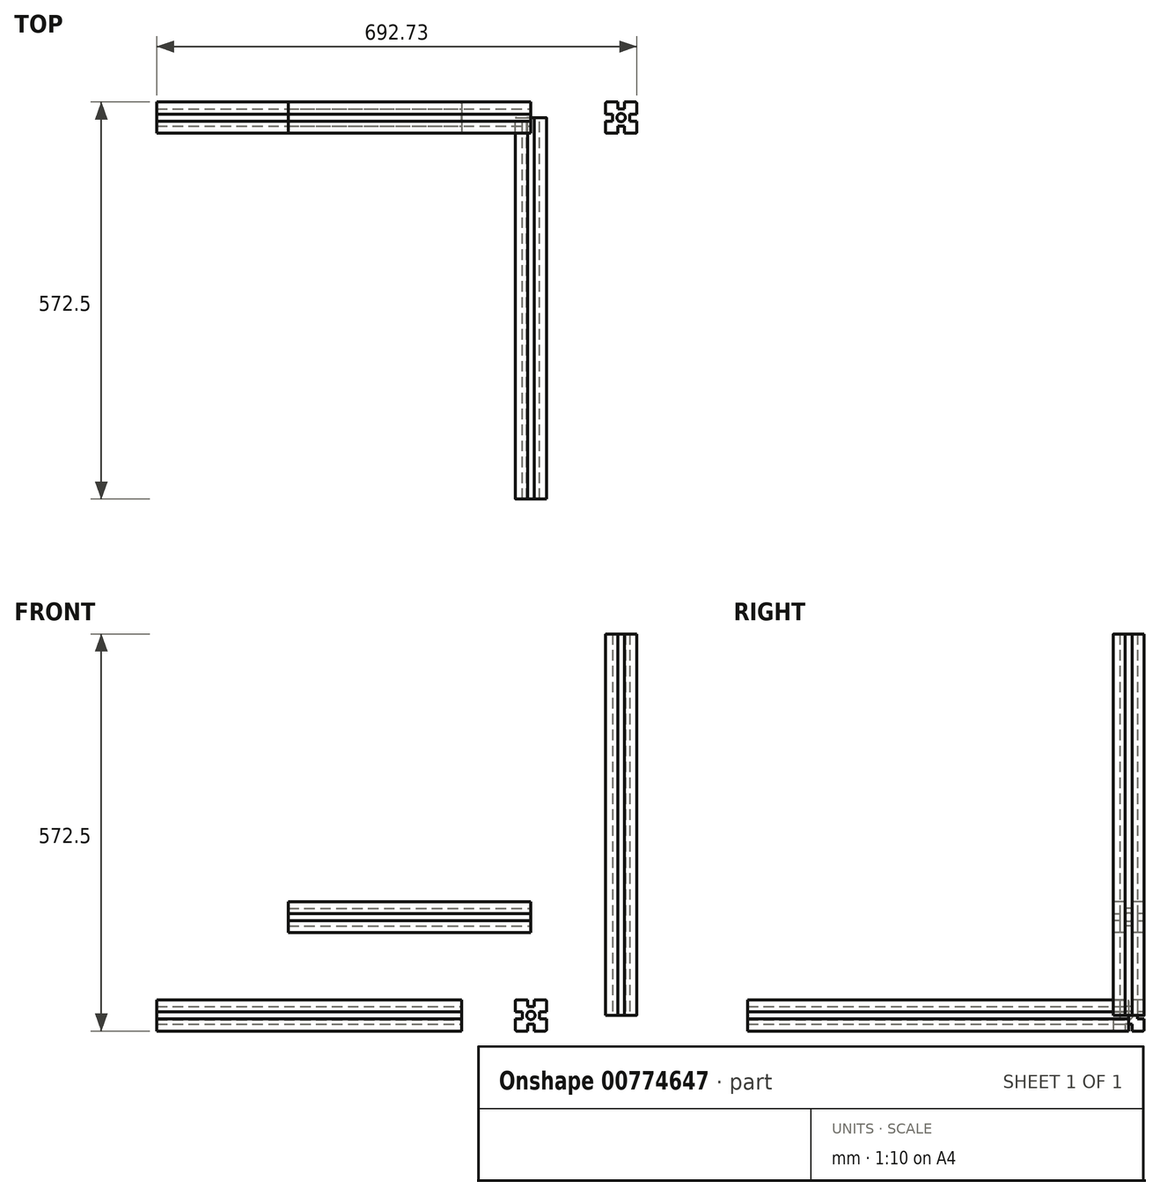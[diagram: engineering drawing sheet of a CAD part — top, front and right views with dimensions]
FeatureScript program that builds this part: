
annotation { "Feature Type Name" : "Feature", "Feature Type Description" : "" }
export const myFeature = defineFeature(function(context is Context, id is Id, definition is map)
    precondition{}
    {
        {
            var Q0;
            Q0=qCreatedBy(makeId("Front.planeOp"),FACE);
            var sketch = newSketch(context, id + "F0", { "sketchPlane" : qUnion([Q0])});
            skLineSegment(sketch, "E0.bottom", {"start": v(-20.5, 22.5) * mm, "end": v(-5, 22.5) * mm});
            skLineSegment(sketch, "E0.top", {"start": v(-20.5, -22.5) * mm, "end": v(-5, -22.5) * mm});
            skLineSegment(sketch, "E0.left", {"start": v(-22.5, 20.5) * mm, "end": v(-22.5, 5) * mm});
            skLineSegment(sketch, "E0.right", {"start": v(22.5, 20.5) * mm, "end": v(22.5, 5) * mm});
            skPoint(sketch, "E1.visualSharp", {"position": v(-22.5, 22.5) * mm});
            skArc(sketch, "E1.filletArc", {"start": v(-20.5, 22.5) * mm, "mid": v(-21.91, 21.91) * mm, "end": v(-22.5, 20.5) * mm});
            skPoint(sketch, "E2.visualSharp", {"position": v(22.5, 22.5) * mm});
            skArc(sketch, "E2.filletArc", {"start": v(22.5, 20.5) * mm, "mid": v(21.91, 21.91) * mm, "end": v(20.5, 22.5) * mm});
            skPoint(sketch, "E3.visualSharp", {"position": v(22.5, -22.5) * mm});
            skArc(sketch, "E3.filletArc", {"start": v(20.5, -22.5) * mm, "mid": v(21.91, -21.91) * mm, "end": v(22.5, -20.5) * mm});
            skPoint(sketch, "E4.visualSharp", {"position": v(-22.5, -22.5) * mm});
            skArc(sketch, "E4.filletArc", {"start": v(-22.5, -20.5) * mm, "mid": v(-21.91, -21.91) * mm, "end": v(-20.5, -22.5) * mm});
            skLineSegment(sketch, "E5", {"start": v(-5, 22.5) * mm, "end": v(-5, 12.5) * mm});
            skLineSegment(sketch, "E6", {"start": v(-5, 12.5) * mm, "end": v(5, 12.5) * mm});
            skLineSegment(sketch, "E7", {"start": v(5, 12.5) * mm, "end": v(5, 22.5) * mm});
            skLineSegment(sketch, "E8", {"start": v(-22.5, 5) * mm, "end": v(-12.5, 5) * mm});
            skLineSegment(sketch, "E9", {"start": v(-12.5, 5) * mm, "end": v(-12.5, -5) * mm});
            skLineSegment(sketch, "E10", {"start": v(-12.5, -5) * mm, "end": v(-22.5, -5) * mm});
            skLineSegment(sketch, "E11", {"start": v(-5, -22.5) * mm, "end": v(-5, -12.5) * mm});
            skLineSegment(sketch, "E12", {"start": v(-5, -12.5) * mm, "end": v(5, -12.5) * mm});
            skLineSegment(sketch, "E13", {"start": v(5, -12.5) * mm, "end": v(5, -22.5) * mm});
            skLineSegment(sketch, "E14", {"start": v(22.5, 5) * mm, "end": v(12.5, 5) * mm});
            skLineSegment(sketch, "E15", {"start": v(12.5, 5) * mm, "end": v(12.5, -5) * mm});
            skLineSegment(sketch, "E16", {"start": v(12.5, -5) * mm, "end": v(22.5, -5) * mm});
            skCircle(sketch, "E17", {"center": v(0, 0) * mm, "radius": 6 * mm});
            skLineSegment(sketch, "E18.trimOffspring", {"start": v(5, 22.5) * mm, "end": v(20.5, 22.5) * mm});
            skLineSegment(sketch, "E19.trimOffspring", {"start": v(22.5, -5) * mm, "end": v(22.5, -20.5) * mm});
            skLineSegment(sketch, "E20.trimOffspring", {"start": v(5, -22.5) * mm, "end": v(20.5, -22.5) * mm});
            skLineSegment(sketch, "E21.trimOffspring", {"start": v(-22.5, -5) * mm, "end": v(-22.5, -20.5) * mm});
            skSolve(sketch);
        }
        {
            var Q0;
            Q0 = qSketchRegion(id + "F0", true);
            extrude(context, id + "F1", {"entities" : qUnion([Q0]), "depth" : 350 * mm, "offsetDistance" : 25 * mm});
        }
        {
            var Q0;
            Q0 = qSketchRegion(id + "F0", true);
            extrude(context, id + "F2", {"entities" : qUnion([Q0]), "depth" : 550 * mm, "offsetDistance" : 25 * mm});
        }
        {
            var Q0;
            Q0=qCreatedBy(makeId("Front.planeOp"),FACE);
            var sketch = newSketch(context, id + "F3", { "sketchPlane" : qUnion([Q0])});
            skLineSegment(sketch, "E22", {"start": v(0, 71.55) * mm, "end": v(0, -70.15) * mm, "construction": true});
            skLineSegment(sketch, "E23", {"start": v(-68.62, 0) * mm, "end": v(61.61, 0) * mm, "construction": true});
            skSolve(sketch);
        }
        {
            var Q0;
            Q0=makeQuery(id+"F1.opExtrude","SWEPT_BODY",BODY,{"disambiguationData":[OSD([sQuery(id+"F0.wireOp",EDGE,"E0.bottom"),sQuery(id+"F0.wireOp",EDGE,"E0.top"),sQuery(id+"F0.wireOp",EDGE,"E0.left"),sQuery(id+"F0.wireOp",EDGE,"E0.right"),sQuery(id+"F0.wireOp",EDGE,"E1.filletArc"),sQuery(id+"F0.wireOp",EDGE,"E2.filletArc"),sQuery(id+"F0.wireOp",EDGE,"E3.filletArc"),sQuery(id+"F0.wireOp",EDGE,"E4.filletArc"),sQuery(id+"F0.wireOp",EDGE,"E5"),sQuery(id+"F0.wireOp",EDGE,"E6"),sQuery(id+"F0.wireOp",EDGE,"E7"),sQuery(id+"F0.wireOp",EDGE,"E8"),sQuery(id+"F0.wireOp",EDGE,"E9"),sQuery(id+"F0.wireOp",EDGE,"E10"),sQuery(id+"F0.wireOp",EDGE,"E11"),sQuery(id+"F0.wireOp",EDGE,"E12"),sQuery(id+"F0.wireOp",EDGE,"E13"),sQuery(id+"F0.wireOp",EDGE,"E14"),sQuery(id+"F0.wireOp",EDGE,"E15"),sQuery(id+"F0.wireOp",EDGE,"E16"),sQuery(id+"F0.wireOp",EDGE,"E17"),sQuery(id+"F0.wireOp",EDGE,"E18.trimOffspring"),sQuery(id+"F0.wireOp",EDGE,"E19.trimOffspring"),sQuery(id+"F0.wireOp",EDGE,"E20.trimOffspring"),sQuery(id+"F0.wireOp",EDGE,"E21.trimOffspring")])]});
            var Q1;
            Q1=sQuery(id+"F3.wireOp",EDGE,"E22");
            transform(context, id + "F4", {"entities" : qUnion([Q0]), "transformType" : TransformType.ROTATION, "transformAxis" : qUnion([Q1]), "angle" : 90 * degree, "makeCopy" : false});
        }
        {
            var Q0;
            Q0=makeQuery(id+"F1.opExtrude","SWEPT_BODY",BODY,{"disambiguationData":[OSD([sQuery(id+"F0.wireOp",EDGE,"E0.bottom"),sQuery(id+"F0.wireOp",EDGE,"E0.top"),sQuery(id+"F0.wireOp",EDGE,"E0.left"),sQuery(id+"F0.wireOp",EDGE,"E0.right"),sQuery(id+"F0.wireOp",EDGE,"E1.filletArc"),sQuery(id+"F0.wireOp",EDGE,"E2.filletArc"),sQuery(id+"F0.wireOp",EDGE,"E3.filletArc"),sQuery(id+"F0.wireOp",EDGE,"E4.filletArc"),sQuery(id+"F0.wireOp",EDGE,"E5"),sQuery(id+"F0.wireOp",EDGE,"E6"),sQuery(id+"F0.wireOp",EDGE,"E7"),sQuery(id+"F0.wireOp",EDGE,"E8"),sQuery(id+"F0.wireOp",EDGE,"E9"),sQuery(id+"F0.wireOp",EDGE,"E10"),sQuery(id+"F0.wireOp",EDGE,"E11"),sQuery(id+"F0.wireOp",EDGE,"E12"),sQuery(id+"F0.wireOp",EDGE,"E13"),sQuery(id+"F0.wireOp",EDGE,"E14"),sQuery(id+"F0.wireOp",EDGE,"E15"),sQuery(id+"F0.wireOp",EDGE,"E16"),sQuery(id+"F0.wireOp",EDGE,"E17"),sQuery(id+"F0.wireOp",EDGE,"E18.trimOffspring"),sQuery(id+"F0.wireOp",EDGE,"E19.trimOffspring"),sQuery(id+"F0.wireOp",EDGE,"E20.trimOffspring"),sQuery(id+"F0.wireOp",EDGE,"E21.trimOffspring")])]});
            var Q1;
            Q1=sQuery(id+"F3.wireOp",EDGE,"E22");
            transform(context, id + "F5", {"entities" : qUnion([Q0]), "transformType" : TransformType.TRANSLATION_ENTITY, "oppositeDirectionEntity" : true, "transformLine" : qUnion([Q1]), "makeCopy" : false});
        }
        {
            var Q0;
            Q0 = qSketchRegion(id + "F0", true);
            extrude(context, id + "F6", {"entities" : qUnion([Q0]), "depth" : 550 * mm, "offsetDistance" : 25 * mm});
        }
        {
            var Q0;
            Q0=makeQuery(id+"F6.opExtrude","SWEPT_BODY",BODY,{"disambiguationData":[OSD([sQuery(id+"F0.wireOp",EDGE,"E0.bottom"),sQuery(id+"F0.wireOp",EDGE,"E0.top"),sQuery(id+"F0.wireOp",EDGE,"E0.left"),sQuery(id+"F0.wireOp",EDGE,"E0.right"),sQuery(id+"F0.wireOp",EDGE,"E1.filletArc"),sQuery(id+"F0.wireOp",EDGE,"E2.filletArc"),sQuery(id+"F0.wireOp",EDGE,"E3.filletArc"),sQuery(id+"F0.wireOp",EDGE,"E4.filletArc"),sQuery(id+"F0.wireOp",EDGE,"E5"),sQuery(id+"F0.wireOp",EDGE,"E6"),sQuery(id+"F0.wireOp",EDGE,"E7"),sQuery(id+"F0.wireOp",EDGE,"E8"),sQuery(id+"F0.wireOp",EDGE,"E9"),sQuery(id+"F0.wireOp",EDGE,"E10"),sQuery(id+"F0.wireOp",EDGE,"E11"),sQuery(id+"F0.wireOp",EDGE,"E12"),sQuery(id+"F0.wireOp",EDGE,"E13"),sQuery(id+"F0.wireOp",EDGE,"E14"),sQuery(id+"F0.wireOp",EDGE,"E15"),sQuery(id+"F0.wireOp",EDGE,"E16"),sQuery(id+"F0.wireOp",EDGE,"E17"),sQuery(id+"F0.wireOp",EDGE,"E18.trimOffspring"),sQuery(id+"F0.wireOp",EDGE,"E19.trimOffspring"),sQuery(id+"F0.wireOp",EDGE,"E20.trimOffspring"),sQuery(id+"F0.wireOp",EDGE,"E21.trimOffspring")])]});
            var Q1;
            Q1=sQuery(id+"F3.wireOp",EDGE,"E23");
            transform(context, id + "F7", {"entities" : qUnion([Q0]), "transformType" : TransformType.ROTATION, "transformAxis" : qUnion([Q1]), "angle" : 90 * degree, "oppositeDirection" : true, "makeCopy" : false});
        }
        {
            var Q0;
            Q0=makeQuery(id+"F6.opExtrude","SWEPT_BODY",BODY,{"disambiguationData":[OSD([sQuery(id+"F0.wireOp",EDGE,"E0.bottom"),sQuery(id+"F0.wireOp",EDGE,"E0.top"),sQuery(id+"F0.wireOp",EDGE,"E0.left"),sQuery(id+"F0.wireOp",EDGE,"E0.right"),sQuery(id+"F0.wireOp",EDGE,"E1.filletArc"),sQuery(id+"F0.wireOp",EDGE,"E2.filletArc"),sQuery(id+"F0.wireOp",EDGE,"E3.filletArc"),sQuery(id+"F0.wireOp",EDGE,"E4.filletArc"),sQuery(id+"F0.wireOp",EDGE,"E5"),sQuery(id+"F0.wireOp",EDGE,"E6"),sQuery(id+"F0.wireOp",EDGE,"E7"),sQuery(id+"F0.wireOp",EDGE,"E8"),sQuery(id+"F0.wireOp",EDGE,"E9"),sQuery(id+"F0.wireOp",EDGE,"E10"),sQuery(id+"F0.wireOp",EDGE,"E11"),sQuery(id+"F0.wireOp",EDGE,"E12"),sQuery(id+"F0.wireOp",EDGE,"E13"),sQuery(id+"F0.wireOp",EDGE,"E14"),sQuery(id+"F0.wireOp",EDGE,"E15"),sQuery(id+"F0.wireOp",EDGE,"E16"),sQuery(id+"F0.wireOp",EDGE,"E17"),sQuery(id+"F0.wireOp",EDGE,"E18.trimOffspring"),sQuery(id+"F0.wireOp",EDGE,"E19.trimOffspring"),sQuery(id+"F0.wireOp",EDGE,"E20.trimOffspring"),sQuery(id+"F0.wireOp",EDGE,"E21.trimOffspring")])]});
            var Q1;
            Q1=sQuery(id+"F3.wireOp",EDGE,"E23");
            transform(context, id + "F8", {"entities" : qUnion([Q0]), "transformType" : TransformType.TRANSLATION_ENTITY, "oppositeDirectionEntity" : false, "transformLine" : qUnion([Q1]), "makeCopy" : false});
        }
        {
            var Q0;
            Q0=makeQuery(id+"F1.opExtrude","SWEPT_BODY",BODY,{"disambiguationData":[OSD([sQuery(id+"F0.wireOp",EDGE,"E0.bottom"),sQuery(id+"F0.wireOp",EDGE,"E0.top"),sQuery(id+"F0.wireOp",EDGE,"E0.left"),sQuery(id+"F0.wireOp",EDGE,"E0.right"),sQuery(id+"F0.wireOp",EDGE,"E1.filletArc"),sQuery(id+"F0.wireOp",EDGE,"E2.filletArc"),sQuery(id+"F0.wireOp",EDGE,"E3.filletArc"),sQuery(id+"F0.wireOp",EDGE,"E4.filletArc"),sQuery(id+"F0.wireOp",EDGE,"E5"),sQuery(id+"F0.wireOp",EDGE,"E6"),sQuery(id+"F0.wireOp",EDGE,"E7"),sQuery(id+"F0.wireOp",EDGE,"E8"),sQuery(id+"F0.wireOp",EDGE,"E9"),sQuery(id+"F0.wireOp",EDGE,"E10"),sQuery(id+"F0.wireOp",EDGE,"E11"),sQuery(id+"F0.wireOp",EDGE,"E12"),sQuery(id+"F0.wireOp",EDGE,"E13"),sQuery(id+"F0.wireOp",EDGE,"E14"),sQuery(id+"F0.wireOp",EDGE,"E15"),sQuery(id+"F0.wireOp",EDGE,"E16"),sQuery(id+"F0.wireOp",EDGE,"E17"),sQuery(id+"F0.wireOp",EDGE,"E18.trimOffspring"),sQuery(id+"F0.wireOp",EDGE,"E19.trimOffspring"),sQuery(id+"F0.wireOp",EDGE,"E20.trimOffspring"),sQuery(id+"F0.wireOp",EDGE,"E21.trimOffspring")])]});
            transform(context, id + "F9", {"entities" : qUnion([Q0]), "transformType" : TransformType.TRANSLATION_3D, "dx" : 0 * mm, "dy" : -399 * mm, "dz" : 0 * mm, "makeCopy" : true});
        }
        {
            var Q0;
            Q0=makeQuery(id+"F9.opPattern","COPY",BODY,{"derivedFrom":makeQuery(id+"F1.opExtrude","SWEPT_BODY",BODY,{"disambiguationData":[OSD([sQuery(id+"F0.wireOp",EDGE,"E0.bottom"),sQuery(id+"F0.wireOp",EDGE,"E0.top"),sQuery(id+"F0.wireOp",EDGE,"E0.left"),sQuery(id+"F0.wireOp",EDGE,"E0.right"),sQuery(id+"F0.wireOp",EDGE,"E1.filletArc"),sQuery(id+"F0.wireOp",EDGE,"E2.filletArc"),sQuery(id+"F0.wireOp",EDGE,"E3.filletArc"),sQuery(id+"F0.wireOp",EDGE,"E4.filletArc"),sQuery(id+"F0.wireOp",EDGE,"E5"),sQuery(id+"F0.wireOp",EDGE,"E6"),sQuery(id+"F0.wireOp",EDGE,"E7"),sQuery(id+"F0.wireOp",EDGE,"E8"),sQuery(id+"F0.wireOp",EDGE,"E9"),sQuery(id+"F0.wireOp",EDGE,"E10"),sQuery(id+"F0.wireOp",EDGE,"E11"),sQuery(id+"F0.wireOp",EDGE,"E12"),sQuery(id+"F0.wireOp",EDGE,"E13"),sQuery(id+"F0.wireOp",EDGE,"E14"),sQuery(id+"F0.wireOp",EDGE,"E15"),sQuery(id+"F0.wireOp",EDGE,"E16"),sQuery(id+"F0.wireOp",EDGE,"E17"),sQuery(id+"F0.wireOp",EDGE,"E18.trimOffspring"),sQuery(id+"F0.wireOp",EDGE,"E19.trimOffspring"),sQuery(id+"F0.wireOp",EDGE,"E20.trimOffspring"),sQuery(id+"F0.wireOp",EDGE,"E21.trimOffspring")])]}),"instanceName":"1"});
            deleteBodies(context, id + "F10", {"entities" : qUnion([Q0])});
        }
        {
            var Q0;
            Q0 = qSketchRegion(id + "F0", true);
            extrude(context, id + "F11", {"entities" : qUnion([Q0]), "depth" : 440 * mm, "offsetDistance" : 25 * mm});
        }
        {
            var Q0;
            Q0=makeQuery(id+"F11.opExtrude","SWEPT_BODY",BODY,{"disambiguationData":[OSD([sQuery(id+"F0.wireOp",EDGE,"E0.bottom"),sQuery(id+"F0.wireOp",EDGE,"E0.top"),sQuery(id+"F0.wireOp",EDGE,"E0.left"),sQuery(id+"F0.wireOp",EDGE,"E0.right"),sQuery(id+"F0.wireOp",EDGE,"E1.filletArc"),sQuery(id+"F0.wireOp",EDGE,"E2.filletArc"),sQuery(id+"F0.wireOp",EDGE,"E3.filletArc"),sQuery(id+"F0.wireOp",EDGE,"E4.filletArc"),sQuery(id+"F0.wireOp",EDGE,"E5"),sQuery(id+"F0.wireOp",EDGE,"E6"),sQuery(id+"F0.wireOp",EDGE,"E7"),sQuery(id+"F0.wireOp",EDGE,"E8"),sQuery(id+"F0.wireOp",EDGE,"E9"),sQuery(id+"F0.wireOp",EDGE,"E10"),sQuery(id+"F0.wireOp",EDGE,"E11"),sQuery(id+"F0.wireOp",EDGE,"E12"),sQuery(id+"F0.wireOp",EDGE,"E13"),sQuery(id+"F0.wireOp",EDGE,"E14"),sQuery(id+"F0.wireOp",EDGE,"E15"),sQuery(id+"F0.wireOp",EDGE,"E16"),sQuery(id+"F0.wireOp",EDGE,"E17"),sQuery(id+"F0.wireOp",EDGE,"E18.trimOffspring"),sQuery(id+"F0.wireOp",EDGE,"E19.trimOffspring"),sQuery(id+"F0.wireOp",EDGE,"E20.trimOffspring"),sQuery(id+"F0.wireOp",EDGE,"E21.trimOffspring")])]});
            var Q1;
            Q1=sQuery(id+"F3.wireOp",EDGE,"E22");
            transform(context, id + "F12", {"entities" : qUnion([Q0]), "transformType" : TransformType.ROTATION, "transformAxis" : qUnion([Q1]), "angle" : 90 * degree, "makeCopy" : false});
        }
        {
            var Q0;
            Q0=makeQuery(id+"F11.opExtrude","SWEPT_BODY",BODY,{"disambiguationData":[OSD([sQuery(id+"F0.wireOp",EDGE,"E0.bottom"),sQuery(id+"F0.wireOp",EDGE,"E0.top"),sQuery(id+"F0.wireOp",EDGE,"E0.left"),sQuery(id+"F0.wireOp",EDGE,"E0.right"),sQuery(id+"F0.wireOp",EDGE,"E1.filletArc"),sQuery(id+"F0.wireOp",EDGE,"E2.filletArc"),sQuery(id+"F0.wireOp",EDGE,"E3.filletArc"),sQuery(id+"F0.wireOp",EDGE,"E4.filletArc"),sQuery(id+"F0.wireOp",EDGE,"E5"),sQuery(id+"F0.wireOp",EDGE,"E6"),sQuery(id+"F0.wireOp",EDGE,"E7"),sQuery(id+"F0.wireOp",EDGE,"E8"),sQuery(id+"F0.wireOp",EDGE,"E9"),sQuery(id+"F0.wireOp",EDGE,"E10"),sQuery(id+"F0.wireOp",EDGE,"E11"),sQuery(id+"F0.wireOp",EDGE,"E12"),sQuery(id+"F0.wireOp",EDGE,"E13"),sQuery(id+"F0.wireOp",EDGE,"E14"),sQuery(id+"F0.wireOp",EDGE,"E15"),sQuery(id+"F0.wireOp",EDGE,"E16"),sQuery(id+"F0.wireOp",EDGE,"E17"),sQuery(id+"F0.wireOp",EDGE,"E18.trimOffspring"),sQuery(id+"F0.wireOp",EDGE,"E19.trimOffspring"),sQuery(id+"F0.wireOp",EDGE,"E20.trimOffspring"),sQuery(id+"F0.wireOp",EDGE,"E21.trimOffspring")])]});
            var Q1;
            Q1=makeQuery(id+"F11.opExtrude","CAP_VERTEX",VERTEX,{"disambiguationData":[OSD([sQuery(id+"F0.wireOp",EDGE,"E0.right"),sQuery(id+"F0.wireOp",EDGE,"E14")])],"isStart":false});
            var Q2;
            Q2=sQuery(id+"F3.wireOp",EDGE,"E23");
            transform(context, id + "F13", {"entities" : qUnion([Q0]), "transformType" : TransformType.TRANSLATION_DISTANCE, "transformDirection" : qUnion([Q2]), "distance" : 100 * mm, "oppositeDirection" : true, "makeCopy" : false});
        }
    });
